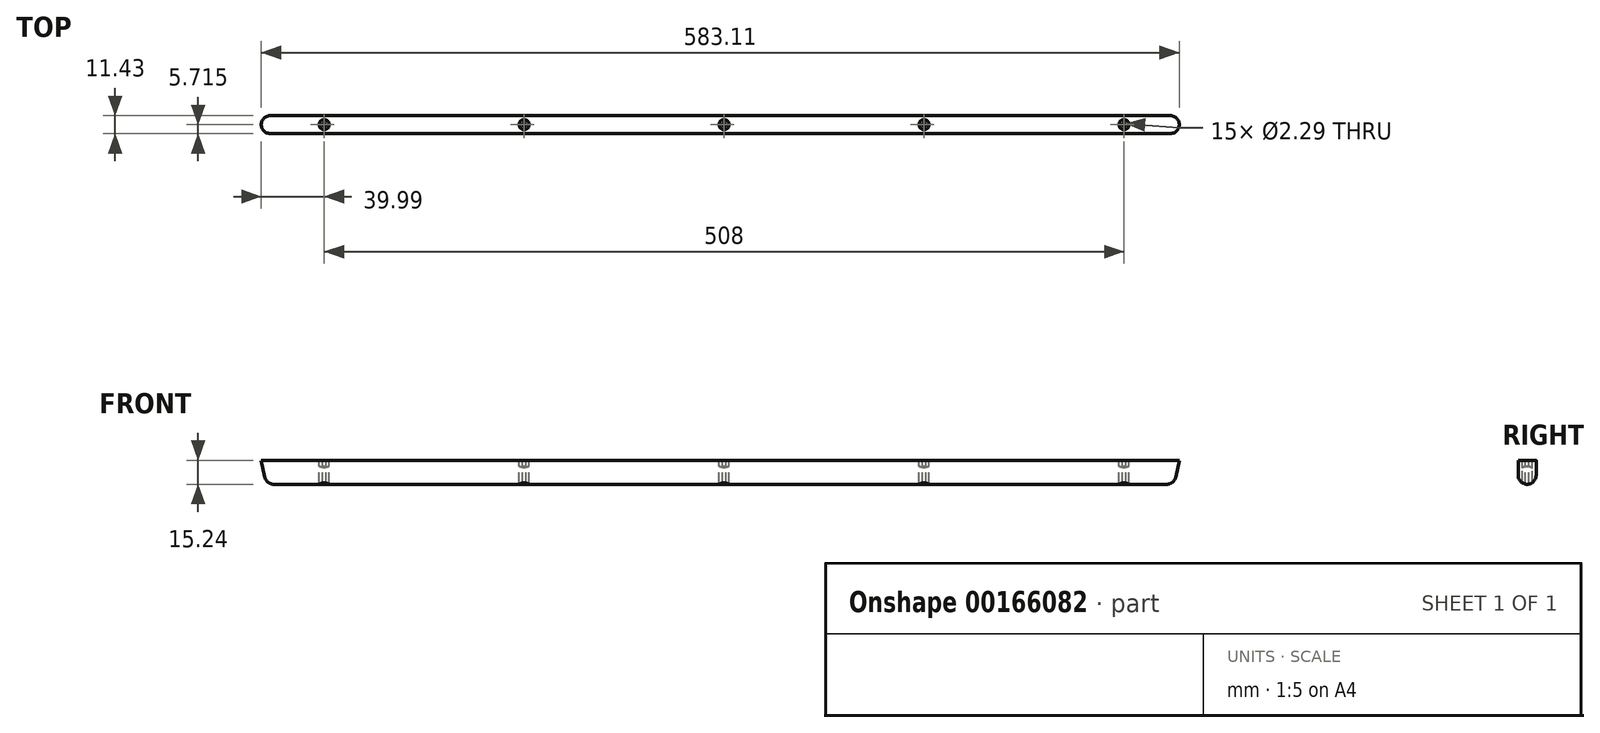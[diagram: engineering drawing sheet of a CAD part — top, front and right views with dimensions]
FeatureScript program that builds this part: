
annotation { "Feature Type Name" : "Feature", "Feature Type Description" : "" }
export const myFeature = defineFeature(function(context is Context, id is Id, definition is map)
    precondition{}
    {
        {
            var Q0;
            Q0=qCreatedBy(makeId("Front.planeOp"),FACE);
            var sketch = newSketch(context, id + "F0", { "sketchPlane" : qUnion([Q0])});
            skLineSegment(sketch, "E0", {"start": v(-294.54, 0) * mm, "end": v(289.66, 0) * mm});
            skLineSegment(sketch, "E1", {"start": v(-290.73, -17.78) * mm, "end": v(285.85, -17.78) * mm});
            skLineSegment(sketch, "E2", {"start": v(285.85, -17.78) * mm, "end": v(289.66, 0) * mm});
            skLineSegment(sketch, "E3", {"start": v(-290.73, -17.78) * mm, "end": v(-294.54, 0) * mm});
            skSolve(sketch);
        }
        {
            var Q0;
            Q0=makeQuery(id+"F0.imprint","IMPRINT",FACE,{"disambiguationData":[TD([[makeQuery(id+"F0.imprint","IMPRINT",EDGE,{"derivedFrom":sQuery(id+"F0.wireOp",EDGE,"E0")}),-1.0]])]});
            extrude(context, id + "F1", {"entities" : qUnion([Q0]), "depth" : 11.43 * mm});
        }
        {
            var Q0;
            Q0=makeQuery(id+"F1.opExtrude","CAP_EDGE",EDGE,{"disambiguationData":[OSD([sQuery(id+"F0.wireOp",EDGE,"E1")])],"isStart":true});
            var Q1;
            Q1=makeQuery(id+"F1.opExtrude","CAP_EDGE",EDGE,{"disambiguationData":[OSD([sQuery(id+"F0.wireOp",EDGE,"E1")])],"isStart":false});
            fillet(context, id + "F2", {"entities" : qUnion([Q0, Q1]), "radius" : 5.7 * mm, "tangentPropagation" : true, "allowEdgeOverflow" : false});
        }
        {
            var Q0;
            Q0=makeQuery(id+"F1.opExtrude","CAP_EDGE",EDGE,{"disambiguationData":[OSD([sQuery(id+"F0.wireOp",EDGE,"E2")])],"isStart":true});
            var Q1;
            Q1=makeQuery(id+"F1.opExtrude","CAP_EDGE",EDGE,{"disambiguationData":[OSD([sQuery(id+"F0.wireOp",EDGE,"E2")])],"isStart":false});
            var Q2;
            Q2=makeQuery(id+"F2.opFillet","BLEND_EDGE",EDGE,{"blendedFrom":[makeQuery(id+"F1.opExtrude","CAP_EDGE",EDGE,{"disambiguationData":[OSD([sQuery(id+"F0.wireOp",EDGE,"E1")])],"isStart":true}),makeQuery(id+"F1.opExtrude","SWEPT_FACE",FACE,{"disambiguationData":[OSD([sQuery(id+"F0.wireOp",EDGE,"E2")])]})],"blendedInto":[makeQuery(id+"F1.opExtrude","SWEPT_FACE",FACE,{"disambiguationData":[OSD([sQuery(id+"F0.wireOp",EDGE,"E2")])]})]});
            var Q3;
            Q3=makeQuery(id+"F2.opFillet","BLEND_EDGE",EDGE,{"blendedFrom":[makeQuery(id+"F1.opExtrude","CAP_EDGE",EDGE,{"disambiguationData":[OSD([sQuery(id+"F0.wireOp",EDGE,"E1")])],"isStart":false}),makeQuery(id+"F1.opExtrude","SWEPT_FACE",FACE,{"disambiguationData":[OSD([sQuery(id+"F0.wireOp",EDGE,"E2")])]})],"blendedInto":[makeQuery(id+"F1.opExtrude","SWEPT_FACE",FACE,{"disambiguationData":[OSD([sQuery(id+"F0.wireOp",EDGE,"E2")])]})]});
            var Q4;
            Q4=makeQuery(id+"F1.opExtrude","SWEPT_EDGE",EDGE,{"disambiguationData":[OSD([sQuery(id+"F0.wireOp",EDGE,"E1"),sQuery(id+"F0.wireOp",EDGE,"E2")])]});
            fillet(context, id + "F3", {"entities" : qUnion([Q0, Q1, Q2, Q3, Q4]), "radius" : 5.7 * mm, "tangentPropagation" : true, "allowEdgeOverflow" : false});
        }
        {
            var Q0;
            Q0=makeQuery(id+"F1.opExtrude","CAP_EDGE",EDGE,{"disambiguationData":[OSD([sQuery(id+"F0.wireOp",EDGE,"E3")])],"isStart":false});
            var Q1;
            Q1=makeQuery(id+"F1.opExtrude","CAP_EDGE",EDGE,{"disambiguationData":[OSD([sQuery(id+"F0.wireOp",EDGE,"E3")])],"isStart":true});
            var Q2;
            Q2=makeQuery(id+"F2.opFillet","BLEND_EDGE",EDGE,{"blendedFrom":[makeQuery(id+"F1.opExtrude","CAP_EDGE",EDGE,{"disambiguationData":[OSD([sQuery(id+"F0.wireOp",EDGE,"E1")])],"isStart":false}),makeQuery(id+"F1.opExtrude","SWEPT_FACE",FACE,{"disambiguationData":[OSD([sQuery(id+"F0.wireOp",EDGE,"E3")])]})],"blendedInto":[makeQuery(id+"F1.opExtrude","SWEPT_FACE",FACE,{"disambiguationData":[OSD([sQuery(id+"F0.wireOp",EDGE,"E3")])]})]});
            var Q3;
            Q3=makeQuery(id+"F1.opExtrude","SWEPT_EDGE",EDGE,{"disambiguationData":[OSD([sQuery(id+"F0.wireOp",EDGE,"E1"),sQuery(id+"F0.wireOp",EDGE,"E3")])]});
            var Q4;
            Q4=makeQuery(id+"F2.opFillet","BLEND_EDGE",EDGE,{"blendedFrom":[makeQuery(id+"F1.opExtrude","CAP_EDGE",EDGE,{"disambiguationData":[OSD([sQuery(id+"F0.wireOp",EDGE,"E1")])],"isStart":true}),makeQuery(id+"F1.opExtrude","SWEPT_FACE",FACE,{"disambiguationData":[OSD([sQuery(id+"F0.wireOp",EDGE,"E3")])]})],"blendedInto":[makeQuery(id+"F1.opExtrude","SWEPT_FACE",FACE,{"disambiguationData":[OSD([sQuery(id+"F0.wireOp",EDGE,"E3")])]})]});
            fillet(context, id + "F4", {"entities" : qUnion([Q0, Q1, Q2, Q3, Q4]), "radius" : 5.7 * mm, "tangentPropagation" : true, "allowEdgeOverflow" : false});
        }
        {
            var Q0;
            Q0=makeQuery(id+"F1.opExtrude","SWEPT_FACE",FACE,{"disambiguationData":[OSD([sQuery(id+"F0.wireOp",EDGE,"E0")])]});
            var sketch = newSketch(context, id + "F5", { "sketchPlane" : qUnion([Q0])});
            skPoint(sketch, "E4", {"position": v(0, -11.43) * mm});
            skPoint(sketch, "E5", {"position": v(0, -5.72) * mm});
            skCircle(sketch, "E6", {"center": v(0, -5.72) * mm, "radius": 1.14 * mm});
            skCircle(sketch, "E7", {"center": v(0, -5.72) * mm, "radius": 3.2 * mm});
            skCircle(sketch, "E8.1.0.0", {"center": v(127, -5.72) * mm, "radius": 1.14 * mm});
            skCircle(sketch, "E8.1.0.1", {"center": v(127, -5.72) * mm, "radius": 3.2 * mm});
            skCircle(sketch, "E8.2.0.0", {"center": v(254, -5.72) * mm, "radius": 1.14 * mm});
            skCircle(sketch, "E8.2.0.1", {"center": v(254, -5.72) * mm, "radius": 3.2 * mm});
            skLineSegment(sketch, "E8.direction1", {"start": v(0, -5.72) * mm, "end": v(127, -5.72) * mm, "construction": true});
            skCircle(sketch, "E9.1.0.0", {"center": v(-127, -5.72) * mm, "radius": 3.2 * mm});
            skCircle(sketch, "E9.1.0.1", {"center": v(-127, -5.72) * mm, "radius": 1.14 * mm});
            skCircle(sketch, "E9.2.0.0", {"center": v(-254, -5.72) * mm, "radius": 3.2 * mm});
            skCircle(sketch, "E9.2.0.1", {"center": v(-254, -5.72) * mm, "radius": 1.14 * mm});
            skLineSegment(sketch, "E9.direction1", {"start": v(0, -5.72) * mm, "end": v(-127, -5.72) * mm, "construction": true});
            skSolve(sketch);
        }
        {
            var Q0;
            Q0 = qSketchRegion(id + "F5", true);
            var Q1;
            Q1=sQuery(id+"F5.wireOp",EDGE,"E8.1.0.1");
            var Q2;
            Q2=sQuery(id+"F5.wireOp",EDGE,"E7");
            var Q3;
            Q3=sQuery(id+"F5.wireOp",EDGE,"E9.1.0.0");
            var Q4;
            Q4=sQuery(id+"F5.wireOp",EDGE,"E9.2.0.0");
            var Q5;
            Q5=sQuery(id+"F5.wireOp",EDGE,"E8.2.0.1");
            var Q6;
            Q6=makeQuery(id+"F2.opFillet","BLEND_FACE",FACE,{"disambiguationData":[OSD([sQuery(id+"F0.wireOp",EDGE,"E1")])]});
            var Q7;
            Q7=makeQuery(id+"F1.opExtrude","SWEPT_BODY",BODY,{"disambiguationData":[OSD([sQuery(id+"F0.wireOp",EDGE,"E0"),sQuery(id+"F0.wireOp",EDGE,"E1"),sQuery(id+"F0.wireOp",EDGE,"E2"),sQuery(id+"F0.wireOp",EDGE,"E3")])]});
            var Q8;
            Q8=makeQuery(id+"F2.opFillet","BLEND_FACE",FACE,{"disambiguationData":[OSD([sQuery(id+"F0.wireOp",EDGE,"E1")])]});
            extrude(context, id + "F6", {"entities" : qUnion([Q0]), "surfaceEntities" : qUnion([Q1, Q2, Q3, Q4, Q5]), "endBound" : BoundingType.UP_TO_BODY, "oppositeDirection" : true, "endBoundEntityFace" : qUnion([Q6]), "endBoundEntityBody" : qUnion([Q7]), "depth" : 25.4 * mm, "hasSecondDirection" : true, "secondDirectionBound" : SecondDirectionBoundingType.UP_TO_SURFACE, "secondDirectionOppositeDirection" : true, "secondDirectionBoundEntityFace" : qUnion([Q8]), "secondDirectionDepth" : 25.4 * mm});
        }
        {
            var Q0;
            Q0=makeQuery(id+"F5.imprint","IMPRINT",FACE,{"disambiguationData":[TD([[makeQuery(id+"F5.imprint","IMPRINT",EDGE,{"derivedFrom":sQuery(id+"F5.wireOp",EDGE,"E8.1.0.0")}),1.0]])]});
            var Q1;
            Q1=makeQuery(id+"F5.imprint","IMPRINT",FACE,{"disambiguationData":[TD([[makeQuery(id+"F5.imprint","IMPRINT",EDGE,{"derivedFrom":sQuery(id+"F5.wireOp",EDGE,"E8.2.0.0")}),1.0]])]});
            var Q2;
            Q2=makeQuery(id+"F5.imprint","IMPRINT",FACE,{"disambiguationData":[TD([[makeQuery(id+"F5.imprint","IMPRINT",EDGE,{"derivedFrom":sQuery(id+"F5.wireOp",EDGE,"E6")}),1.0]])]});
            var Q3;
            Q3=makeQuery(id+"F5.imprint","IMPRINT",FACE,{"disambiguationData":[TD([[makeQuery(id+"F5.imprint","IMPRINT",EDGE,{"derivedFrom":sQuery(id+"F5.wireOp",EDGE,"E9.1.0.1")}),1.0]])]});
            var Q4;
            Q4=makeQuery(id+"F5.imprint","IMPRINT",FACE,{"disambiguationData":[TD([[makeQuery(id+"F5.imprint","IMPRINT",EDGE,{"derivedFrom":sQuery(id+"F5.wireOp",EDGE,"E9.2.0.1")}),1.0]])]});
            var Q5;
            Q5=makeQuery(id+"F2.opFillet","BLEND_FACE",FACE,{"disambiguationData":[OSD([sQuery(id+"F0.wireOp",EDGE,"E1")])]});
            extrude(context, id + "F7", {"entities" : qUnion([Q0, Q1, Q2, Q3, Q4]), "operationType" : NewBodyOperationType.REMOVE, "endBound" : BoundingType.UP_TO_SURFACE, "oppositeDirection" : true, "endBoundEntityFace" : qUnion([Q5]), "depth" : 25.4 * mm});
        }
        {
            var Q0;
            Q0 = qSketchRegion(id + "F5", true);
            var Q1;
            Q1 = qConstructionFilter(qBodyType(qCreatedBy(id + "F5" ,EDGE), BodyType.WIRE), ConstructionObject.NO);
            var Q2;
            Q2=makeQuery(id+"F2.opFillet","BLEND_FACE",FACE,{"disambiguationData":[OSD([sQuery(id+"F0.wireOp",EDGE,"E1")])]});
            extrude(context, id + "F8", {"entities" : qUnion([Q0]), "surfaceEntities" : qUnion([Q1]), "endBound" : BoundingType.UP_TO_SURFACE, "oppositeDirection" : true, "endBoundEntityFace" : qUnion([Q2]), "depth" : 7.62 * mm});
        }
        {
            var Q0;
            Q0=makeQuery(id+"F1.opExtrude","SWEPT_FACE",FACE,{"disambiguationData":[OSD([sQuery(id+"F0.wireOp",EDGE,"E0")])]});
            extrude(context, id + "F9", {"entities" : qUnion([Q0]), "operationType" : NewBodyOperationType.REMOVE, "oppositeDirection" : true, "depth" : 2.54 * mm});
        }
    });
